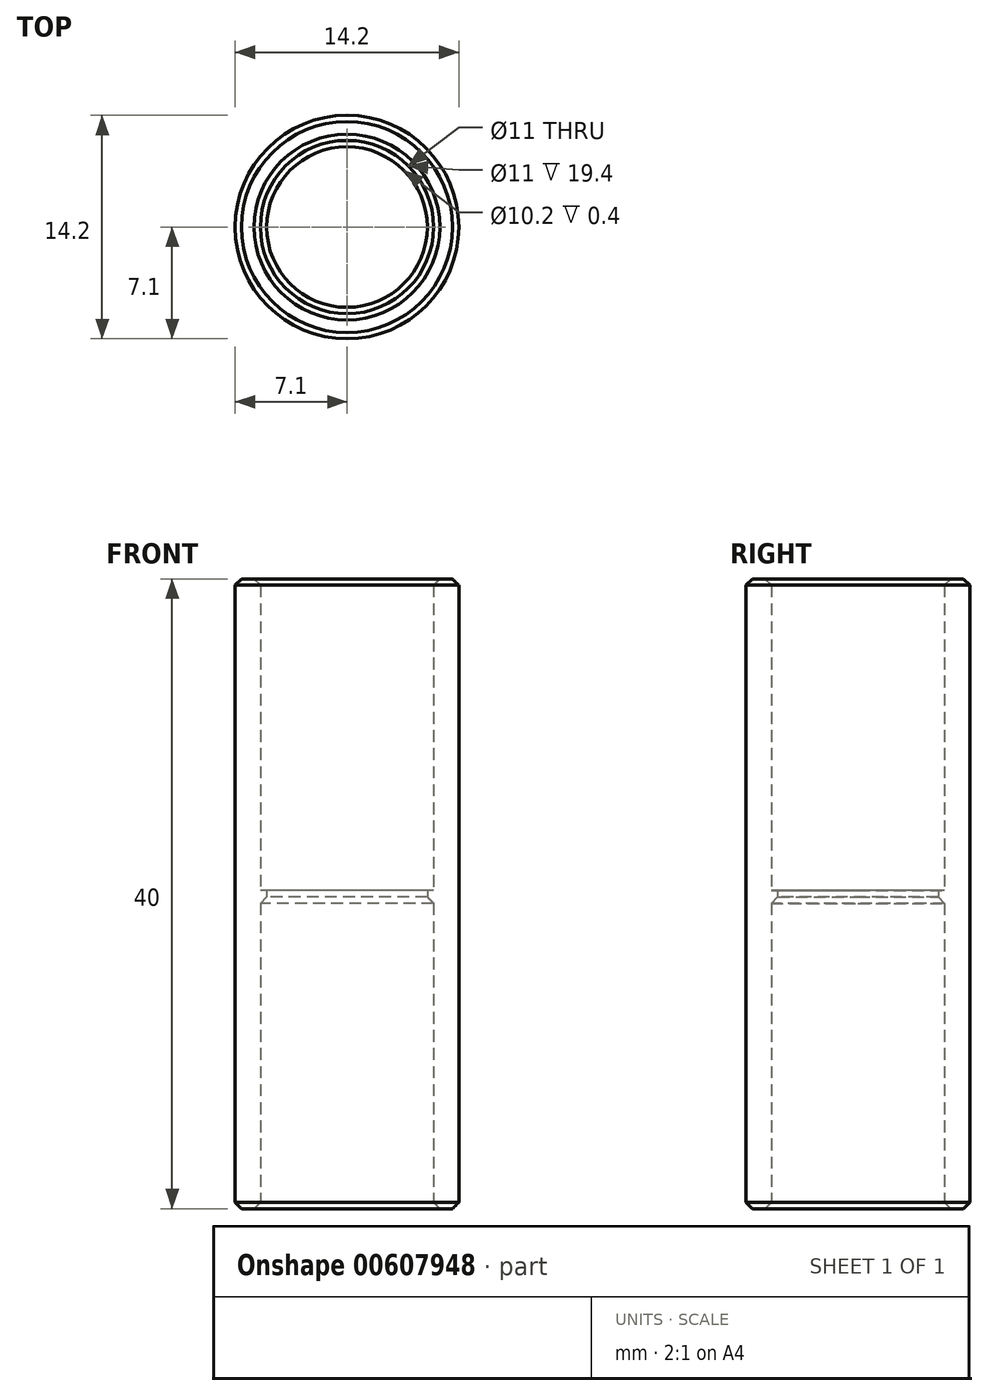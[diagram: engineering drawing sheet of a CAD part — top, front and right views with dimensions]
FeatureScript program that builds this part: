
annotation { "Feature Type Name" : "Feature", "Feature Type Description" : "" }
export const myFeature = defineFeature(function(context is Context, id is Id, definition is map)
    precondition{}
    {
        {
            var Q0;
            Q0=qCreatedBy(makeId("Top.planeOp"),FACE);
            var sketch = newSketch(context, id + "F0", { "sketchPlane" : qUnion([Q0])});
            skCircle(sketch, "E0", {"center": v(0, 0) * mm, "radius": 7.1 * mm});
            skCircle(sketch, "E1", {"center": v(0, 0) * mm, "radius": 5.5 * mm});
            skCircle(sketch, "E2", {"center": v(0, 0) * mm, "radius": 5.1 * mm});
            skSolve(sketch);
        }
        {
            var Q0;
            Q0=makeQuery(id+"F0.imprint","IMPRINT",FACE,{"disambiguationData":[TD([[makeQuery(id+"F0.imprint","IMPRINT",EDGE,{"derivedFrom":sQuery(id+"F0.wireOp",EDGE,"E0")}),1.0]])]});
            extrude(context, id + "F1", {"entities" : qUnion([Q0]), "depth" : 40 * mm, "offsetDistance" : 25 * mm});
        }
        {
            var Q0;
            Q0=makeQuery(id+"F0.imprint","IMPRINT",FACE,{"disambiguationData":[TD([[makeQuery(id+"F0.imprint","IMPRINT",EDGE,{"derivedFrom":sQuery(id+"F0.wireOp",EDGE,"E1")}),1.0]])]});
            extrude(context, id + "F2", {"entities" : qUnion([Q0]), "operationType" : NewBodyOperationType.ADD, "depth" : 20.2 * mm, "offsetDistance" : 25 * mm, "hasSecondDirection" : true, "secondDirectionOppositeDirection" : false, "secondDirectionDepth" : 19.8 * mm});
        }
        {
            var Q0;
            Q0=makeQuery(id+"F2.opExtrude","CAP_EDGE",EDGE,{"disambiguationData":[OSD([sQuery(id+"F0.wireOp",EDGE,"E1")])],"isStart":true});
            var Q1;
            Q1=makeQuery(id+"F2.opExtrude","CAP_EDGE",EDGE,{"disambiguationData":[OSD([sQuery(id+"F0.wireOp",EDGE,"E1")])],"isStart":false});
            chamfer(context, id + "F3", {"entities" : qUnion([Q0, Q1]), "width" : .4 * mm, "tangentPropagation" : true});
        }
        {
            var Q0;
            Q0=makeQuery(id+"F1.opExtrude","CAP_EDGE",EDGE,{"disambiguationData":[OSD([sQuery(id+"F0.wireOp",EDGE,"E1")])],"isStart":false});
            var Q1;
            Q1=makeQuery(id+"F1.opExtrude","CAP_EDGE",EDGE,{"disambiguationData":[OSD([sQuery(id+"F0.wireOp",EDGE,"E0")])],"isStart":false});
            var Q2;
            Q2=makeQuery(id+"F1.opExtrude","CAP_EDGE",EDGE,{"disambiguationData":[OSD([sQuery(id+"F0.wireOp",EDGE,"E1")])],"isStart":true});
            var Q3;
            Q3=makeQuery(id+"F1.opExtrude","CAP_EDGE",EDGE,{"disambiguationData":[OSD([sQuery(id+"F0.wireOp",EDGE,"E0")])],"isStart":true});
            chamfer(context, id + "F4", {"entities" : qUnion([Q0, Q1, Q2, Q3]), "width" : .4 * mm, "tangentPropagation" : true});
        }
    });
